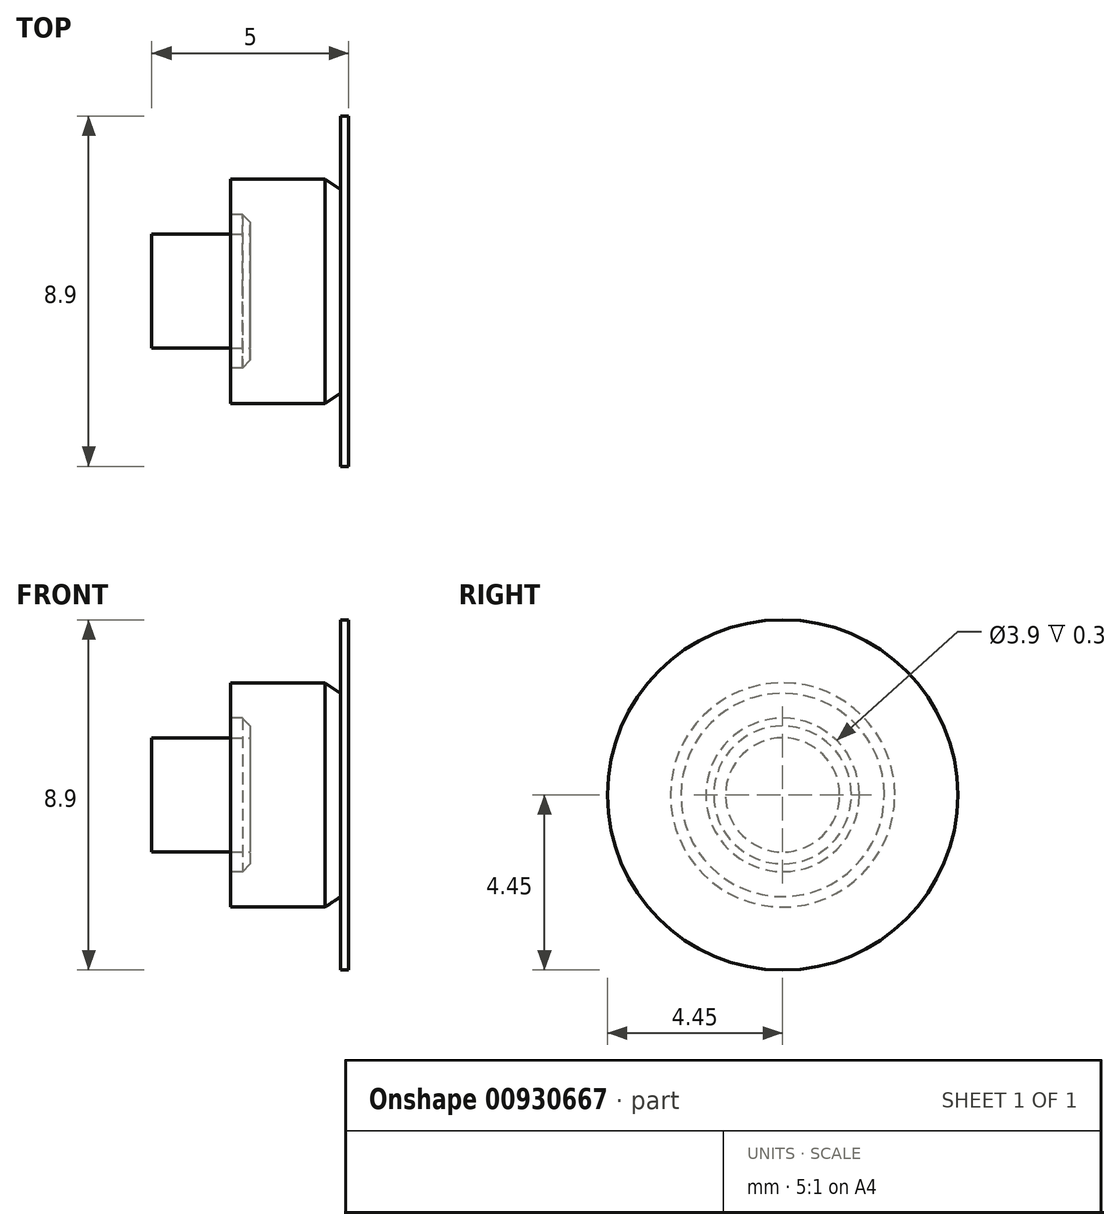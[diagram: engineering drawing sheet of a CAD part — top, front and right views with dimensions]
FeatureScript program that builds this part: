
annotation { "Feature Type Name" : "Feature", "Feature Type Description" : "" }
export const myFeature = defineFeature(function(context is Context, id is Id, definition is map)
    precondition{}
    {
        {
            var Q0;
            Q0=qCreatedBy(makeId("Right.planeOp"),FACE);
            var sketch = newSketch(context, id + "F0", { "sketchPlane" : qUnion([Q0])});
            skCircle(sketch, "E0", {"center": v(0, 0) * mm, "radius": 2.85 * mm});
            skSolve(sketch);
        }
        {
            var Q0;
            Q0=qSketchRegion(id+"F0",true);
            extrude(context, id + "F1", {"entities" : qUnion([Q0]), "depth" : 3 * mm, "offsetDistance" : 25 * mm});
        }
        {
            var Q0;
            Q0=makeQuery(id+"F1.opExtrude","CAP_EDGE",EDGE,{"disambiguationData":[OSD([sQuery(id+"F0.wireOp",EDGE,"E0")])],"isStart":false});
            chamfer(context, id + "F2", {"entities" : qUnion([Q0]), "chamferType" : ChamferType.TWO_OFFSETS, "width1" : 0.4 * mm, "oppositeDirection" : false, "width2" : 0.6 * mm, "tangentPropagation" : true});
        }
        {
            var Q0;
            Q0=makeQuery(id+"F1.opExtrude","CAP_FACE",FACE,{"disambiguationData":[OSD([sQuery(id+"F0.wireOp",EDGE,"E0")])],"isStart":true});
            var sketch = newSketch(context, id + "F3", { "sketchPlane" : qUnion([Q0])});
            skCircle(sketch, "E1", {"center": v(0, 0) * mm, "radius": 1.45 * mm});
            skSolve(sketch);
        }
        {
            var Q0;
            Q0=qSketchRegion(id+"F3",true);
            extrude(context, id + "F4", {"entities" : qUnion([Q0]), "operationType" : NewBodyOperationType.ADD, "depth" : 2 * mm, "offsetDistance" : 25 * mm});
        }
        {
            var Q0;
            Q0=makeQuery(id+"F1.opExtrude","CAP_FACE",FACE,{"disambiguationData":[OSD([sQuery(id+"F0.wireOp",EDGE,"E0")])],"isStart":true});
            var sketch = newSketch(context, id + "F5", { "sketchPlane" : qUnion([Q0])});
            skCircle(sketch, "E2", {"center": v(0, 0) * mm, "radius": 1.95 * mm});
            skCircle(sketch, "E3", {"center": v(0, 0) * mm, "radius": 1.45 * mm});
            skSolve(sketch);
        }
        {
            var Q0;
            Q0=qSketchRegion(id+"F5",true);
            extrude(context, id + "F6", {"entities" : qUnion([Q0]), "operationType" : NewBodyOperationType.REMOVE, "oppositeDirection" : true, "depth" : 0.5 * mm, "offsetDistance" : 25 * mm});
        }
        {
            var Q0;
            Q0=makeQuery(id+"F6.boolean.opBoolean","COPY",EDGE,{"derivedFrom":makeQuery(id+"F6.opExtrude","CAP_EDGE",EDGE,{"disambiguationData":[OSD([sQuery(id+"F5.wireOp",EDGE,"E2")])],"isStart":false})});
            chamfer(context, id + "F7", {"entities" : qUnion([Q0]), "width" : 0.2 * mm, "tangentPropagation" : true});
        }
        {
            var Q0;
            Q0=makeQuery(id+"F1.opExtrude","CAP_FACE",FACE,{"disambiguationData":[OSD([sQuery(id+"F0.wireOp",EDGE,"E0")])],"isStart":false});
            var sketch = newSketch(context, id + "F8", { "sketchPlane" : qUnion([Q0])});
            skCircle(sketch, "E4", {"center": v(0, 0) * mm, "radius": 4.45 * mm});
            skCircle(sketch, "E5", {"center": v(0, 0) * mm, "radius": 2.45 * mm});
            skSolve(sketch);
        }
        {
            var Q0;
            Q0=qSketchRegion(id+"F8",true);
            extrude(context, id + "F9", {"entities" : qUnion([Q0]), "operationType" : NewBodyOperationType.ADD, "oppositeDirection" : true, "depth" : 0.2 * mm, "offsetDistance" : 25 * mm});
        }
    });
